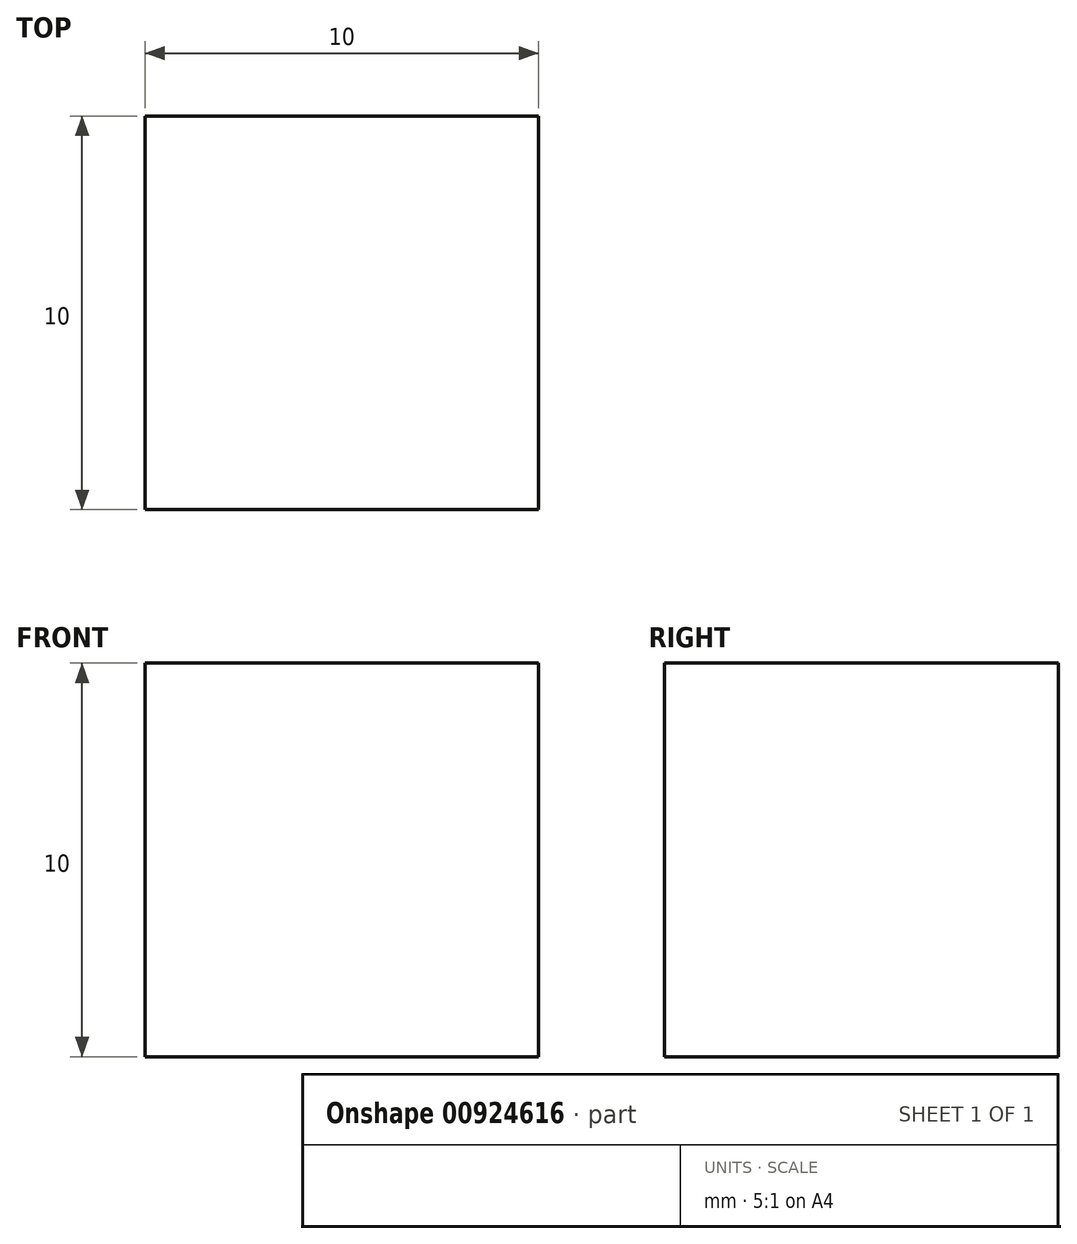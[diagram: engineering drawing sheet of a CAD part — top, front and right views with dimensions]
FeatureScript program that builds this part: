
annotation { "Feature Type Name" : "Feature", "Feature Type Description" : "" }
export const myFeature = defineFeature(function(context is Context, id is Id, definition is map)
    precondition{}
    {
        {
            var Q0;
            Q0=qCreatedBy(makeId("Top.planeOp"),FACE);
            var sketch = newSketch(context, id + "F0", { "sketchPlane" : qUnion([Q0])});
            skLineSegment(sketch, "E0", {"start": v(0, 0) * mm, "end": v(10, 0) * mm});
            skLineSegment(sketch, "E1", {"start": v(10, 0) * mm, "end": v(10, 10) * mm});
            skLineSegment(sketch, "E2", {"start": v(10, 10) * mm, "end": v(0, 10) * mm});
            skLineSegment(sketch, "E3", {"start": v(0, 10) * mm, "end": v(0, 0) * mm});
            skSolve(sketch);
        }
        {
            var Q0;
            Q0=makeQuery(id+"F0.imprint","IMPRINT",FACE,{"disambiguationData":[TD([[makeQuery(id+"F0.imprint","IMPRINT",EDGE,{"derivedFrom":sQuery(id+"F0.wireOp",EDGE,"E0")}),1.0]])]});
            extrude(context, id + "F1", {"entities" : qUnion([Q0]), "depth" : 10 * mm, "offsetDistance" : 25 * mm});
        }
    });
